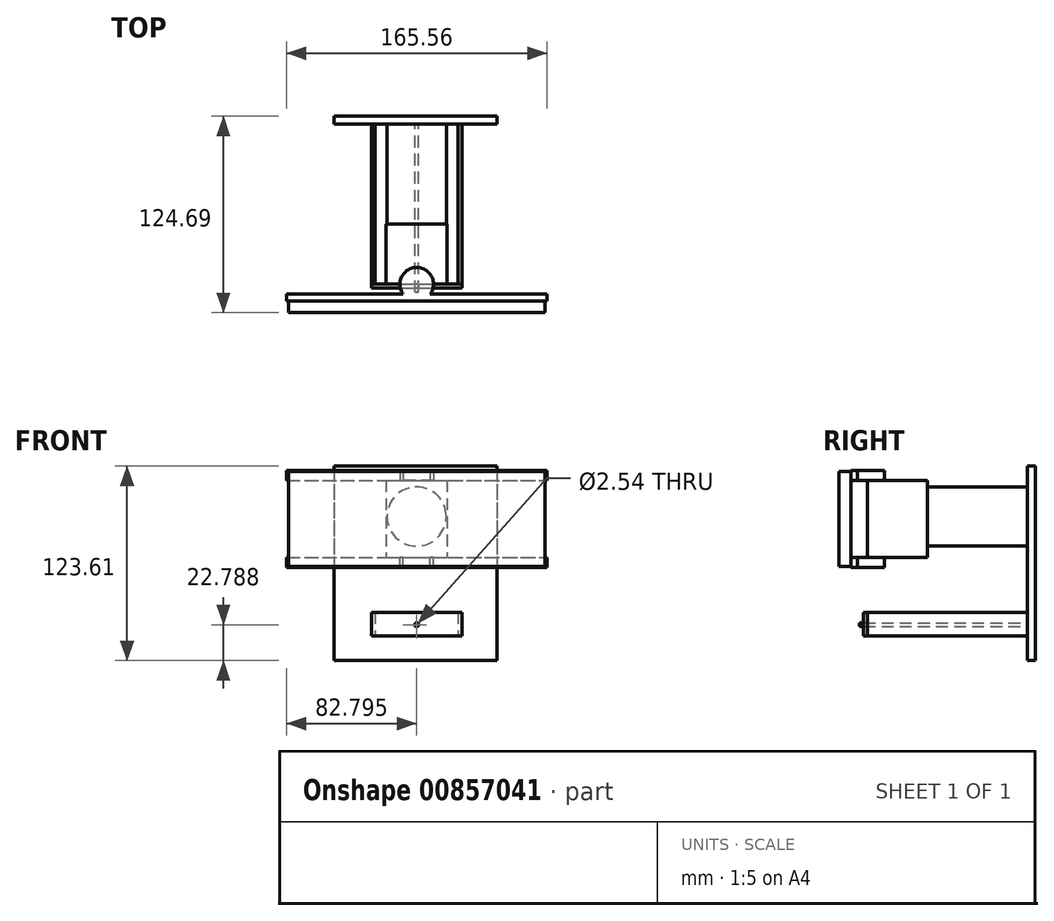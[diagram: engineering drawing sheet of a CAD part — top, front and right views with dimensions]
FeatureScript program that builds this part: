
annotation { "Feature Type Name" : "Feature", "Feature Type Description" : "" }
export const myFeature = defineFeature(function(context is Context, id is Id, definition is map)
    precondition{}
    {
        {
            var Q0;
            Q0=qCreatedBy(makeId("Front.planeOp"),FACE);
            var sketch = newSketch(context, id + "F0", { "sketchPlane" : qUnion([Q0])});
            skLineSegment(sketch, "E0.bottom", {"start": v(-52.45, 58.13) * mm, "end": v(51.11, 58.13) * mm});
            skLineSegment(sketch, "E0.top", {"start": v(-52.45, -65.48) * mm, "end": v(51.11, -65.48) * mm});
            skLineSegment(sketch, "E0.left", {"start": v(-52.45, 58.13) * mm, "end": v(-52.45, -65.48) * mm});
            skLineSegment(sketch, "E0.right", {"start": v(51.11, 58.13) * mm, "end": v(51.11, -65.48) * mm});
            skSolve(sketch);
        }
        {
            var Q0;
            Q0=makeQuery(id+"F0.imprint","IMPRINT",FACE,{"disambiguationData":[TD([[makeQuery(id+"F0.imprint","IMPRINT",EDGE,{"derivedFrom":sQuery(id+"F0.wireOp",EDGE,"E0.bottom")}),-1.0]])]});
            extrude(context, id + "F1", {"entities" : qUnion([Q0]), "depth" : 5.08 * mm, "offsetDistance" : 25.4 * mm});
        }
        {
            var Q0;
            Q0=makeQuery(id+"F1.opExtrude","CAP_FACE",FACE,{"disambiguationData":[OSD([sQuery(id+"F0.wireOp",EDGE,"E0.bottom"),sQuery(id+"F0.wireOp",EDGE,"E0.top"),sQuery(id+"F0.wireOp",EDGE,"E0.left"),sQuery(id+"F0.wireOp",EDGE,"E0.right")])],"isStart":false});
            var sketch = newSketch(context, id + "F2", { "sketchPlane" : qUnion([Q0])});
            skCircle(sketch, "E1", {"center": v(0, 26.06) * mm, "radius": 18.8 * mm});
            skSolve(sketch);
        }
        {
            var Q0;
            Q0=makeQuery(id+"F2.imprint","IMPRINT",FACE,{"disambiguationData":[TD([[makeQuery(id+"F2.imprint","IMPRINT",EDGE,{"derivedFrom":sQuery(id+"F2.wireOp",EDGE,"E1")}),1.0]])]});
            extrude(context, id + "F3", {"entities" : qUnion([Q0]), "depth" : 63.5 * mm, "offsetDistance" : 25.4 * mm});
        }
        {
            var Q0;
            Q0=makeQuery(id+"F3.opExtrude","CAP_FACE",FACE,{"disambiguationData":[OSD([sQuery(id+"F2.wireOp",EDGE,"E1")])],"isStart":false});
            var sketch = newSketch(context, id + "F4", { "sketchPlane" : qUnion([Q0])});
            skLineSegment(sketch, "E2.bottom", {"start": v(-19.38, 49.1) * mm, "end": v(19.38, 49.1) * mm});
            skLineSegment(sketch, "E2.top", {"start": v(-19.38, 0) * mm, "end": v(19.38, 0) * mm});
            skLineSegment(sketch, "E2.left", {"start": v(-19.38, 49.1) * mm, "end": v(-19.38, 0) * mm});
            skLineSegment(sketch, "E2.right", {"start": v(19.38, 49.1) * mm, "end": v(19.38, 0) * mm});
            skSolve(sketch);
        }
        {
            var Q0;
            Q0 = qSketchRegion(id + "F4", true);
            extrude(context, id + "F5", {"entities" : qUnion([Q0]), "operationType" : NewBodyOperationType.ADD, "depth" : 38.1 * mm, "offsetDistance" : 25.4 * mm});
        }
        {
            var Q0;
            Q0=makeQuery(id+"F1.opExtrude","CAP_FACE",FACE,{"disambiguationData":[OSD([sQuery(id+"F0.wireOp",EDGE,"E0.bottom"),sQuery(id+"F0.wireOp",EDGE,"E0.top"),sQuery(id+"F0.wireOp",EDGE,"E0.left"),sQuery(id+"F0.wireOp",EDGE,"E0.right")])],"isStart":false});
            var sketch = newSketch(context, id + "F6", { "sketchPlane" : qUnion([Q0])});
            skLineSegment(sketch, "E3.bottom", {"start": v(-28.73, -34.74) * mm, "end": v(-26.4, -34.74) * mm});
            skLineSegment(sketch, "E3.top", {"start": v(-28.73, -49.78) * mm, "end": v(-26.4, -49.78) * mm});
            skLineSegment(sketch, "E3.left", {"start": v(-28.73, -34.74) * mm, "end": v(-28.73, -49.78) * mm});
            skLineSegment(sketch, "E3.right", {"start": v(-26.4, -34.74) * mm, "end": v(-26.4, -49.78) * mm});
            skLineSegment(sketch, "E4.MirrorCS", {"start": v(28.73, -34.74) * mm, "end": v(26.4, -34.74) * mm});
            skLineSegment(sketch, "E5.MirrorCS", {"start": v(26.4, -34.74) * mm, "end": v(26.4, -49.78) * mm});
            skLineSegment(sketch, "E6.MirrorCS", {"start": v(28.73, -34.74) * mm, "end": v(28.73, -49.78) * mm});
            skLineSegment(sketch, "E7.MirrorCS", {"start": v(28.73, -49.78) * mm, "end": v(26.4, -49.78) * mm});
            skSolve(sketch);
        }
        {
            var Q0;
            Q0 = qSketchRegion(id + "F6", true);
            extrude(context, id + "F7", {"entities" : qUnion([Q0]), "operationType" : NewBodyOperationType.ADD, "depth" : 101.6 * mm, "offsetDistance" : 25.4 * mm});
        }
        {
            var Q0;
            Q0=makeQuery(id+"F7.opExtrude","SWEPT_FACE",FACE,{"disambiguationData":[OSD([sQuery(id+"F6.wireOp",EDGE,"E6.MirrorCS")])]});
            var sketch = newSketch(context, id + "F8", { "sketchPlane" : qUnion([Q0])});
            skLineSegment(sketch, "E8.bottom", {"start": v(-106.68, -49.78) * mm, "end": v(-109.12, -49.78) * mm});
            skLineSegment(sketch, "E8.top", {"start": v(-106.68, -34.7) * mm, "end": v(-109.12, -34.7) * mm});
            skLineSegment(sketch, "E8.left", {"start": v(-106.68, -49.78) * mm, "end": v(-106.68, -34.7) * mm});
            skLineSegment(sketch, "E8.right", {"start": v(-109.12, -49.78) * mm, "end": v(-109.12, -34.7) * mm});
            skSolve(sketch);
        }
        {
            var Q0;
            Q0 = qSketchRegion(id + "F8", true);
            extrude(context, id + "F9", {"entities" : qUnion([Q0]), "oppositeDirection" : true, "depth" : 57.43 * mm, "offsetDistance" : 25.4 * mm});
        }
        {
            var Q0;
            Q0=makeQuery(id+"F9.opExtrude","SWEPT_FACE",FACE,{"disambiguationData":[OSD([sQuery(id+"F8.wireOp",EDGE,"E8.right")])]});
            var sketch = newSketch(context, id + "F10", { "sketchPlane" : qUnion([Q0])});
            skCircle(sketch, "E9", {"center": v(0.02, -42.7) * mm, "radius": 2.22 * mm});
            skPoint(sketch, "E9.centerSnap0", {"position": v(0.02, -49.78) * mm});
            skSolve(sketch);
        }
        {
            var Q0;
            Q0=sQuery(id+"F10.wireOp",VERTEX,"E9.center");
            var Q1;
            Q1=makeQuery(id+"F9.opExtrude","SWEPT_BODY",BODY,{"disambiguationData":[OSD([sQuery(id+"F8.wireOp",EDGE,"E8.bottom"),sQuery(id+"F8.wireOp",EDGE,"E8.top"),sQuery(id+"F8.wireOp",EDGE,"E8.left"),sQuery(id+"F8.wireOp",EDGE,"E8.right")])]});
            hole(context, id + "F11", {"style" : HoleStyle.SIMPLE, "endStyle" : HoleEndStyle.THROUGH, "holeDiameter" : 2.54 * mm, "majorDiameter" : 6.35 * mm, "isTappedThrough" : true, "tappedDepth" : 12.7 * mm, "tapClearance" : 3, "locations" : qUnion([Q0]), "scope" : qUnion([Q1])});
        }
        {
            var Q0;
            Q0=makeQuery(id+"F5.opExtrude","SWEPT_FACE",FACE,{"disambiguationData":[OSD([sQuery(id+"F4.wireOp",EDGE,"E2.bottom")])]});
            var sketch = newSketch(context, id + "F12", { "sketchPlane" : qUnion([Q0])});
            skCircle(sketch, "E10", {"center": v(0, -106.68) * mm, "radius": 10.65 * mm});
            skSolve(sketch);
        }
        {
            var Q0;
            {var subQ0=sQuery(id+"F12.wireOp",EDGE,"E10");var subQ1=makeQuery(id+"F5.opExtrude","CAP_EDGE",EDGE,{"disambiguationData":[OSD([sQuery(id+"F4.wireOp",EDGE,"E2.bottom")])],"isStart":false});var subQ2=makeQuery(id+"F12.imprint","INTERSECT",VERTEX,{"disambiguationData":[OD(0.0)],"derivedFrom":[subQ1,subQ0]});Q0=makeQuery(id+"F12.imprint","IMPRINT",FACE,{"disambiguationData":[TD([[makeQuery(id+"F12.imprint","IMPRINT",EDGE,{"disambiguationData":[TD([[subQ2,-1.0]])],"derivedFrom":subQ0}),1.0]])]});}
            var Q1;
            {var subQ0=sQuery(id+"F12.wireOp",EDGE,"E10");var subQ1=makeQuery(id+"F5.opExtrude","CAP_EDGE",EDGE,{"disambiguationData":[OSD([sQuery(id+"F4.wireOp",EDGE,"E2.bottom")])],"isStart":false});var subQ2=makeQuery(id+"F12.imprint","INTERSECT",VERTEX,{"disambiguationData":[OD(0.0)],"derivedFrom":[subQ1,subQ0]});Q1=makeQuery(id+"F12.imprint","IMPRINT",FACE,{"disambiguationData":[TD([[makeQuery(id+"F12.imprint","IMPRINT",EDGE,{"disambiguationData":[TD([[subQ2,1.0]])],"derivedFrom":subQ0}),1.0]])]});}
            extrude(context, id + "F13", {"entities" : qUnion([Q0, Q1]), "operationType" : NewBodyOperationType.ADD, "depth" : 6.35 * mm, "offsetDistance" : 25.4 * mm});
        }
        {
            var Q0;
            Q0=makeQuery(id+"F5.opExtrude","SWEPT_FACE",FACE,{"disambiguationData":[OSD([sQuery(id+"F4.wireOp",EDGE,"E2.top")])]});
            var sketch = newSketch(context, id + "F14", { "sketchPlane" : qUnion([Q0])});
            skCircle(sketch, "E11", {"center": v(0, 106.68) * mm, "radius": 10.64 * mm});
            skSolve(sketch);
        }
        {
            var Q0;
            {var subQ0=sQuery(id+"F14.wireOp",EDGE,"E11");var subQ1=makeQuery(id+"F5.opExtrude","CAP_EDGE",EDGE,{"disambiguationData":[OSD([sQuery(id+"F4.wireOp",EDGE,"E2.top")])],"isStart":false});var subQ2=makeQuery(id+"F14.imprint","INTERSECT",VERTEX,{"disambiguationData":[OD(0.0)],"derivedFrom":[subQ1,subQ0]});Q0=makeQuery(id+"F14.imprint","IMPRINT",FACE,{"disambiguationData":[TD([[makeQuery(id+"F14.imprint","IMPRINT",EDGE,{"disambiguationData":[TD([[subQ2,-1.0]])],"derivedFrom":subQ0}),1.0]])]});}
            var Q1;
            {var subQ0=sQuery(id+"F14.wireOp",EDGE,"E11");var subQ1=makeQuery(id+"F5.opExtrude","CAP_EDGE",EDGE,{"disambiguationData":[OSD([sQuery(id+"F4.wireOp",EDGE,"E2.top")])],"isStart":false});var subQ2=makeQuery(id+"F14.imprint","INTERSECT",VERTEX,{"disambiguationData":[OD(0.0)],"derivedFrom":[subQ1,subQ0]});Q1=makeQuery(id+"F14.imprint","IMPRINT",FACE,{"disambiguationData":[TD([[makeQuery(id+"F14.imprint","IMPRINT",EDGE,{"disambiguationData":[TD([[subQ2,1.0]])],"derivedFrom":subQ0}),1.0]])]});}
            extrude(context, id + "F15", {"entities" : qUnion([Q0, Q1]), "operationType" : NewBodyOperationType.ADD, "depth" : 6.35 * mm, "offsetDistance" : 25.4 * mm});
        }
        {
            var Q0;
            Q0=makeQuery(id+"F15.opExtrude","CAP_FACE",FACE,{"disambiguationData":[OSD([sQuery(id+"F14.wireOp",EDGE,"E11")])],"isStart":true});
            var sketch = newSketch(context, id + "F16", { "sketchPlane" : qUnion([Q0])});
            skPoint(sketch, "E12.middle", {"position": v(0, -115.17) * mm});
            skLineSegment(sketch, "E13.bottom", {"start": v(-82.78, -117.32) * mm, "end": v(82.78, -117.32) * mm});
            skLineSegment(sketch, "E13.top", {"start": v(-82.78, -113.01) * mm, "end": v(82.78, -113.01) * mm});
            skLineSegment(sketch, "E13.left", {"start": v(-82.78, -117.32) * mm, "end": v(-82.78, -113.01) * mm});
            skLineSegment(sketch, "E13.right", {"start": v(82.78, -117.32) * mm, "end": v(82.78, -113.01) * mm});
            skPoint(sketch, "E13.cornerSnap0", {"position": v(0, -117.32) * mm});
            skSolve(sketch);
        }
        {
            var Q0;
            Q0 = qSketchRegion(id + "F16", true);
            extrude(context, id + "F17", {"entities" : qUnion([Q0]), "operationType" : NewBodyOperationType.ADD, "oppositeDirection" : true, "depth" : 6.35 * mm, "offsetDistance" : 25.4 * mm});
        }
        {
            var Q0;
            Q0=makeQuery(id+"F13.opExtrude","CAP_FACE",FACE,{"disambiguationData":[OSD([sQuery(id+"F12.wireOp",EDGE,"E10")])],"isStart":false});
            var sketch = newSketch(context, id + "F18", { "sketchPlane" : qUnion([Q0])});
            skPoint(sketch, "E14.middle", {"position": v(0, -115.17) * mm});
            skLineSegment(sketch, "E15.bottom", {"start": v(-82.78, -117.33) * mm, "end": v(82.78, -117.33) * mm});
            skLineSegment(sketch, "E15.top", {"start": v(-82.78, -113.01) * mm, "end": v(82.78, -113.01) * mm});
            skLineSegment(sketch, "E15.left", {"start": v(-82.78, -117.33) * mm, "end": v(-82.78, -113.01) * mm});
            skLineSegment(sketch, "E15.right", {"start": v(82.78, -117.33) * mm, "end": v(82.78, -113.01) * mm});
            skPoint(sketch, "E15.cornerSnap0", {"position": v(0, -117.33) * mm});
            skSolve(sketch);
        }
        {
            var Q0;
            Q0 = qSketchRegion(id + "F18", true);
            extrude(context, id + "F19", {"entities" : qUnion([Q0]), "operationType" : NewBodyOperationType.ADD, "oppositeDirection" : true, "depth" : 6.35 * mm, "offsetDistance" : 25.4 * mm});
        }
        {
            var Q0;
            Q0=makeQuery(id+"F17.opExtrude","SWEPT_FACE",FACE,{"disambiguationData":[OSD([sQuery(id+"F16.wireOp",EDGE,"E13.bottom")])]});
            var sketch = newSketch(context, id + "F20", { "sketchPlane" : qUnion([Q0])});
            skLineSegment(sketch, "E16.bottom", {"start": v(-81.45, -5.6) * mm, "end": v(81.46, -5.6) * mm});
            skLineSegment(sketch, "E16.top", {"start": v(-81.45, 54.65) * mm, "end": v(81.46, 54.65) * mm});
            skLineSegment(sketch, "E16.left", {"start": v(-81.45, -5.6) * mm, "end": v(-81.45, 54.65) * mm});
            skLineSegment(sketch, "E16.right", {"start": v(81.46, -5.6) * mm, "end": v(81.46, 54.65) * mm});
            skSolve(sketch);
        }
        {
            var Q0;
            Q0 = qSketchRegion(id + "F20", true);
            extrude(context, id + "F21", {"entities" : qUnion([Q0]), "depth" : 7.37 * mm, "offsetDistance" : 25.4 * mm});
        }
        {
            var Q0;
            Q0=makeQuery(id+"F1.opExtrude","CAP_FACE",FACE,{"disambiguationData":[OSD([sQuery(id+"F0.wireOp",EDGE,"E0.bottom"),sQuery(id+"F0.wireOp",EDGE,"E0.top"),sQuery(id+"F0.wireOp",EDGE,"E0.left"),sQuery(id+"F0.wireOp",EDGE,"E0.right")])],"isStart":false});
            var sketch = newSketch(context, id + "F22", { "sketchPlane" : qUnion([Q0])});
            skCircle(sketch, "E17", {"center": v(0, -42.67) * mm, "radius": 1.15 * mm});
            skSolve(sketch);
        }
        {
            var Q0;
            Q0 = qSketchRegion(id + "F22", true);
            extrude(context, id + "F23", {"entities" : qUnion([Q0]), "operationType" : NewBodyOperationType.ADD, "depth" : 106.68 * mm, "offsetDistance" : 25.4 * mm});
        }
    });
